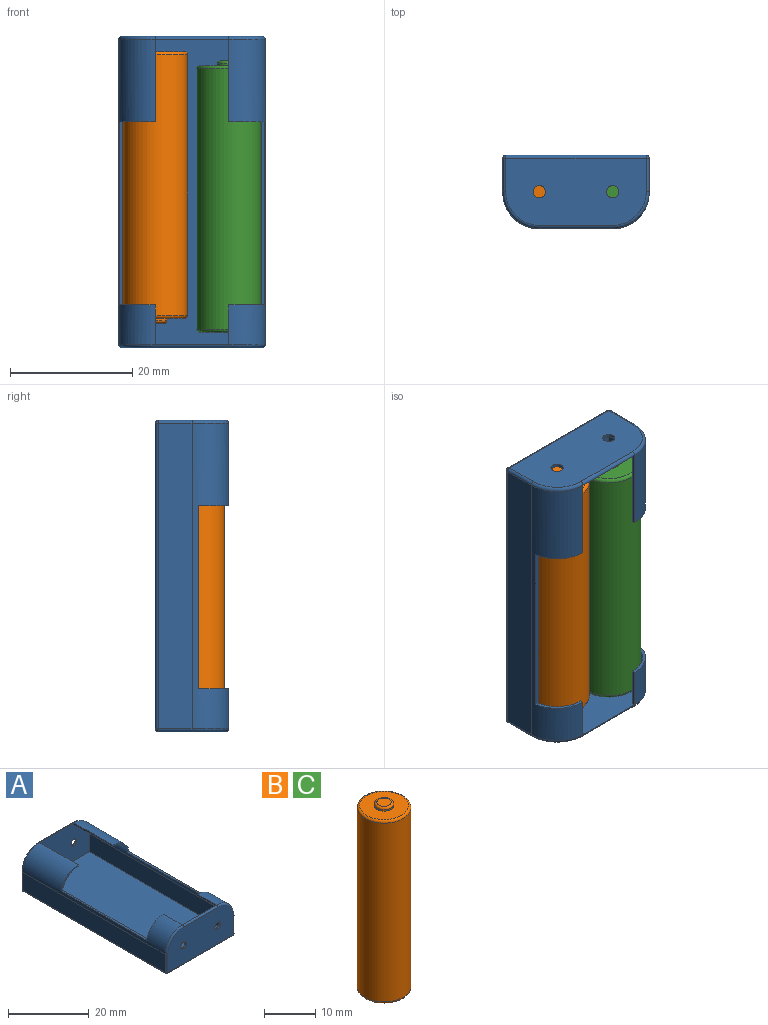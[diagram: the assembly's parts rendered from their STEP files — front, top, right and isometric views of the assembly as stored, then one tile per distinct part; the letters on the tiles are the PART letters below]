
ASSEMBLY  parts=3 mates=2
PART A: 46 faces, bbox 25x51x12.5 mm
  f0: plane 13.5x0.5mm, normal (1,0,0), area 6.8mm2, adj f7,f29,f34,f45
  f1: plane 13.5x0.5mm, normal (-1,0,0), area 6.8mm2, adj f8,f29,f35,f40
  f2: plane 23x11mm, normal (0,1,0), area 233.7mm2, adj f14,f18,f21,f22,f24,f26,f37,f39
  f3: plane 50x5.5mm, normal (-1,0,0), area 275mm2, adj f7,f10,f14,f15
  f4: plane 23x11mm, normal (0,-1,0), area 233.7mm2, adj f9,f10,f11,f13,f16,f17,f36,f38
  f5: plane 50x5.5mm, normal (1,0,0), area 275mm2, adj f8,f17,f23,f26
  f6: plane 50x23mm, normal (0,0,-1), area 1150mm2, adj f15,f16,f22,f23
  f7: cylinder r=6mm len=50mm, axis (0,1,0), area 218.6mm2, adj f0,f3,f9,f18,f27,f43,f44,f45
  f8: cylinder r=6mm len=50mm, axis (0,-1,0), area 218.6mm2, adj f1,f5,f13,f24,f28,f40,f41,f42
  f9: torus R=5.5mm, axis (0,1,0), area 7.2mm2, adj f4,f7,f10,f11
  f10: cylinder r=0.5mm len=5.5mm, axis (0,0,-1), area 4.3mm2, adj f3,f4,f9,f12
  f11: cylinder r=0.5mm len=12mm, axis (-1,0,0), area 9.4mm2, adj f4,f9,f13,f31
  f12: sphere r=0.5mm, area 0.4mm2, adj f10,f15,f16
  f13: torus R=5.5mm, axis (0,1,0), area 7.2mm2, adj f4,f8,f11,f17
  f14: cylinder r=0.5mm len=5.5mm, axis (0,0,1), area 4.3mm2, adj f2,f3,f18,f19
  f15: cylinder r=0.5mm len=50mm, axis (0,-1,0), area 39.3mm2, adj f3,f6,f12,f19
  f16: cylinder r=0.5mm len=23mm, axis (1,0,0), area 18.1mm2, adj f4,f6,f12,f20
  f17: cylinder r=0.5mm len=5.5mm, axis (0,0,1), area 4.3mm2, adj f4,f5,f13,f20
  f18: torus R=5.5mm, axis (0,1,0), area 7.2mm2, adj f2,f7,f14,f21
  f19: sphere r=0.5mm, area 0.4mm2, adj f14,f15,f22
  f20: sphere r=0.5mm, area 0.4mm2, adj f16,f17,f23
  f21: cylinder r=0.5mm len=12mm, axis (1,0,0), area 9.4mm2, adj f2,f18,f24,f29
  f22: cylinder r=0.5mm len=23mm, axis (-1,0,0), area 18.1mm2, adj f2,f6,f19,f25
  f23: cylinder r=0.5mm len=50mm, axis (0,1,0), area 39.3mm2, adj f5,f6,f20,f25
  f24: torus R=5.5mm, axis (0,1,0), area 7.2mm2, adj f2,f8,f21,f26
  f25: sphere r=0.5mm, area 0.4mm2, adj f22,f23,f26
  f26: cylinder r=0.5mm len=5.5mm, axis (0,0,-1), area 4.3mm2, adj f2,f5,f24,f25
  f27: plane 6.5x0.5mm, normal (1,0,0), area 3.3mm2, adj f7,f31,f34,f43
  f28: plane 6.5x0.5mm, normal (-1,0,0), area 3.3mm2, adj f8,f31,f35,f42
  f29: plane 23x11.5mm, normal (0,-1,0), area 239.7mm2, adj f0,f1,f21,f30,f32,f33,f34,f35
  f30: plane 50x5.5mm, normal (1,0,0), area 275mm2, adj f29,f31,f33,f34
  f31: plane 23x11.5mm, normal (0,1,0), area 239.7mm2, adj f11,f27,f28,f30,f32,f33,f34,f35
  f32: plane 50x5.5mm, normal (-1,0,0), area 275mm2, adj f29,f31,f33,f35
  f33: plane 50x23mm, normal (0,0,1), area 1150mm2, adj f29,f30,f31,f32
  f34: cylinder r=5.5mm len=50mm, axis (0,1,0), area 203mm2, adj f0,f27,f29,f30,f31,f43,f44,f45
  f35: cylinder r=5.5mm len=50mm, axis (0,-1,0), area 203mm2, adj f1,f28,f29,f31,f32,f40,f41,f42
  f36: cylinder r=1mm len=2mm, axis (0,-1,0), area 3.1mm2, adj f4,f31
  f37: cylinder r=1mm len=2mm, axis (0,-1,0), area 3.1mm2, adj f2,f29
  f38: cylinder r=1mm len=2mm, axis (0,-1,0), area 3.1mm2, adj f4,f31
  f39: cylinder r=1mm len=2mm, axis (0,-1,0), area 3.1mm2, adj f2,f29
  f40: plane 5.92x5mm, normal (0,-1,0), area 4mm2, adj f1,f8,f35,f41
  f41: plane 30x0.51mm, normal (0,0,1), area 15.2mm2, adj f8,f35,f40,f42
  f42: plane 5.92x5mm, normal (0,1,0), area 4mm2, adj f8,f28,f35,f41
  f43: plane 5.92x5mm, normal (0,1,0), area 4mm2, adj f7,f27,f34,f44
  f44: plane 30x0.51mm, normal (0,0,1), area 15.2mm2, adj f7,f34,f43,f45
  f45: plane 5.92x5mm, normal (0,-1,0), area 4mm2, adj f0,f7,f34,f44
PART B: 8 faces, bbox 11.4x11.4x44.5 mm
  f0: cylinder r=5.25mm len=42.7mm, axis (0,0,-1), area 1408.5mm2, adj f6,f7
  f1: plane 9.5x9.5mm, normal (0,0,-1), area 70.9mm2, adj f7
  f2: cylinder r=1.9mm len=3.8mm, axis (0,0,1), area 3.6mm2, adj f3,f5
  f3: plane 9.5x9.5mm, normal (0,0,1), area 59.5mm2, adj f2,f6
  f4: plane 2.8x2.8mm, normal (0,0,1), area 6.2mm2, adj f5
  f5: torus R=1.4mm, axis (0,0,1), area 8.5mm2, adj f2,f4
  f6: torus R=4.75mm, axis (0,0,1), area 25mm2, adj f0,f3
  f7: torus R=4.75mm, axis (0,0,1), area 25mm2, adj f0,f1
PART C: same geometry as B
PLACE A rot(axis=(1,0,0),90deg) t=(44.81,72.85,5.44)mm
PLACE B rot(axis=(1,0,0),180deg) t=(38.81,66.85,53.94)mm
PLACE C t=(50.81,66.85,7.94)mm
MATE fastened A.f13 <-> C.f0  axis (0,0,1) through (50.81,66.85,5.94)mm
MATE fastened B.f0 <-> A.f9  axis (0,0,1) through (38.81,66.85,53.94)mm
